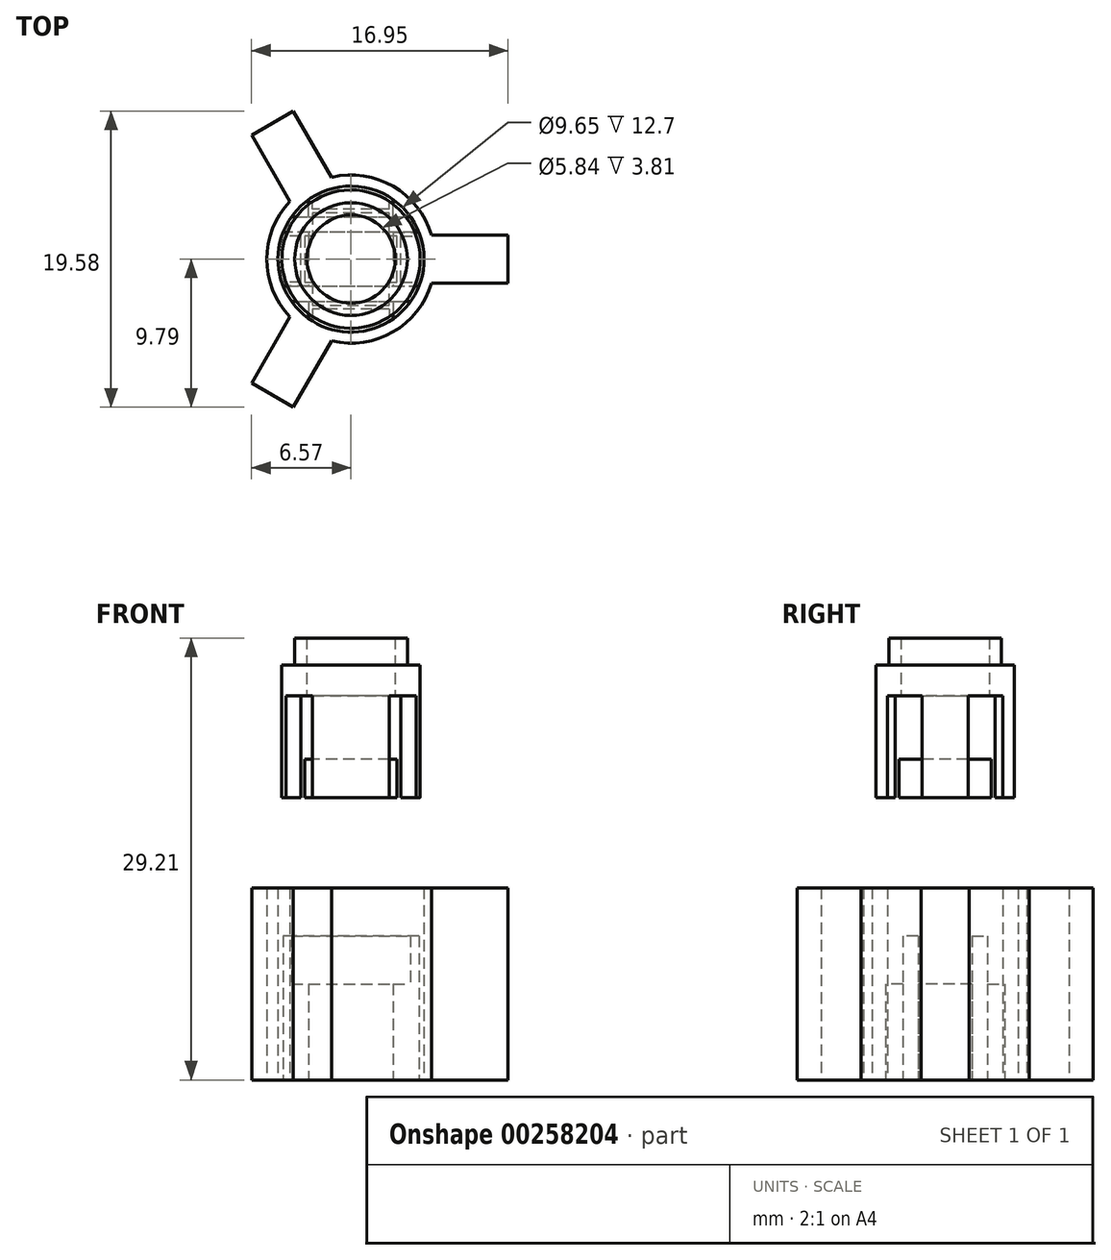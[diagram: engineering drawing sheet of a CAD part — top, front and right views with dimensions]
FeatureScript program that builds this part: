
annotation { "Feature Type Name" : "Feature", "Feature Type Description" : "" }
export const myFeature = defineFeature(function(context is Context, id is Id, definition is map)
    precondition{}
    {
        {
            var Q0;
            Q0=qCreatedBy(makeId("Top.planeOp"),FACE);
            var sketch = newSketch(context, id + "F0", { "sketchPlane" : qUnion([Q0])});
            skCircle(sketch, "E0", {"center": v(0, 0) * mm, "radius": 4.57 * mm});
            skCircle(sketch, "E1", {"center": v(0, 0) * mm, "radius": 2.92 * mm});
            skSolve(sketch);
        }
        {
            var Q0;
            Q0 = qSketchRegion(id + "F0", true);
            extrude(context, id + "F1", {"entities" : qUnion([Q0]), "depth" : 3.8 * mm});
        }
        {
            var Q0;
            Q0=makeQuery(id+"F1.opExtrude","CAP_FACE",FACE,{"disambiguationData":[OSD([sQuery(id+"F0.wireOp",EDGE,"E0"),sQuery(id+"F0.wireOp",EDGE,"E1")])],"isStart":false});
            var sketch = newSketch(context, id + "F2", { "sketchPlane" : qUnion([Q0])});
            skCircle(sketch, "E2.0", {"center": v(0, 0) * mm, "radius": 4.57 * mm});
            skCircle(sketch, "E3", {"center": v(0, 0) * mm, "radius": 3.72 * mm});
            skSolve(sketch);
        }
        {
            var Q0;
            Q0 = qSketchRegion(id + "F2", true);
            extrude(context, id + "F3", {"entities" : qUnion([Q0]), "operationType" : NewBodyOperationType.REMOVE, "oppositeDirection" : true, "depth" : 1.78 * mm});
        }
        {
            var Q0;
            Q0=makeQuery(id+"F1.opExtrude","CAP_FACE",FACE,{"disambiguationData":[OSD([sQuery(id+"F0.wireOp",EDGE,"E0"),sQuery(id+"F0.wireOp",EDGE,"E1")])],"isStart":true});
            var sketch = newSketch(context, id + "F4", { "sketchPlane" : qUnion([Q0])});
            skCircle(sketch, "E4.0", {"center": v(0, 0) * mm, "radius": 2.92 * mm, "construction": true});
            skArc(sketch, "E5.0", {"start": v(-4.31, 1.52) * mm, "mid": v(-4.57, 0) * mm, "end": v(-4.31, -1.52) * mm});
            skLineSegment(sketch, "E6.bottom", {"start": v(-3.3, 3.3) * mm, "end": v(3.3, 3.3) * mm, "construction": true});
            skLineSegment(sketch, "E6.top", {"start": v(-3.3, -3.3) * mm, "end": v(3.3, -3.3) * mm, "construction": true});
            skLineSegment(sketch, "E6.left", {"start": v(-3.3, 3.3) * mm, "end": v(-3.3, -3.3) * mm, "construction": true});
            skLineSegment(sketch, "E6.right", {"start": v(3.3, 3.3) * mm, "end": v(3.3, -3.3) * mm, "construction": true});
            skPoint(sketch, "E7.positionSnap0", {"position": v(-3.3, 0) * mm});
            skPoint(sketch, "E7.positionSnap1", {"position": v(0, 3.3) * mm});
            skLineSegment(sketch, "E8.bottom", {"start": v(-3.3, 1.52) * mm, "end": v(-4.31, 1.52) * mm});
            skLineSegment(sketch, "E8.top", {"start": v(-3.3, -1.52) * mm, "end": v(-4.31, -1.52) * mm});
            skLineSegment(sketch, "E8.left", {"start": v(-3.3, 1.52) * mm, "end": v(-3.3, -1.52) * mm});
            skLineSegment(sketch, "E9.bottom", {"start": v(2.54, 3.3) * mm, "end": v(2.54, 3.8) * mm});
            skLineSegment(sketch, "E9.top", {"start": v(-2.54, 3.3) * mm, "end": v(-2.54, 3.8) * mm});
            skLineSegment(sketch, "E9.left", {"start": v(2.54, 3.3) * mm, "end": v(-2.54, 3.3) * mm});
            skArc(sketch, "E10.trimOffspring", {"start": v(2.54, 3.8) * mm, "mid": v(0, 4.57) * mm, "end": v(-2.54, 3.8) * mm});
            skLineSegment(sketch, "E11", {"start": v(0, 0) * mm, "end": v(-3.3, 0) * mm, "construction": true});
            skLineSegment(sketch, "E12", {"start": v(0, 0) * mm, "end": v(0, 3.3) * mm, "construction": true});
            skPoint(sketch, "E13.MirrorP", {"position": v(3.3, 0) * mm});
            skLineSegment(sketch, "E14.MirrorCS", {"start": v(3.3, 1.52) * mm, "end": v(4.31, 1.52) * mm});
            skLineSegment(sketch, "E15.MirrorCS", {"start": v(3.3, -1.52) * mm, "end": v(4.31, -1.52) * mm});
            skArc(sketch, "E16.MirrorCS", {"start": v(4.31, 1.52) * mm, "mid": v(4.57, 0) * mm, "end": v(4.31, -1.52) * mm});
            skLineSegment(sketch, "E17.MirrorCS", {"start": v(3.3, 1.52) * mm, "end": v(3.3, -1.52) * mm});
            skPoint(sketch, "E18.MirrorP", {"position": v(0, -3.3) * mm});
            skLineSegment(sketch, "E19.MirrorCS", {"start": v(2.54, -3.3) * mm, "end": v(2.54, -3.8) * mm});
            skLineSegment(sketch, "E20.MirrorCS", {"start": v(2.54, -3.3) * mm, "end": v(-2.54, -3.3) * mm});
            skLineSegment(sketch, "E21.MirrorCS", {"start": v(-2.54, -3.3) * mm, "end": v(-2.54, -3.8) * mm});
            skArc(sketch, "E22.MirrorCS", {"start": v(2.54, -3.8) * mm, "mid": v(0, -4.57) * mm, "end": v(-2.54, -3.8) * mm});
            skSolve(sketch);
        }
        {
            var Q0;
            Q0 = qSketchRegion(id + "F4", true);
            extrude(context, id + "F5", {"entities" : qUnion([Q0]), "operationType" : NewBodyOperationType.ADD, "depth" : 3.56 * mm});
        }
        {
            var Q0;
            Q0=makeQuery(id+"F5.opExtrude","CAP_FACE",FACE,{"disambiguationData":[OSD([sQuery(id+"F4.wireOp",EDGE,"E19.MirrorCS"),sQuery(id+"F4.wireOp",EDGE,"E20.MirrorCS"),sQuery(id+"F4.wireOp",EDGE,"E21.MirrorCS"),sQuery(id+"F4.wireOp",EDGE,"E22.MirrorCS")])],"isStart":false});
            var Q1;
            Q1=makeQuery(id+"F5.opExtrude","CAP_FACE",FACE,{"disambiguationData":[OSD([sQuery(id+"F4.wireOp",EDGE,"E9.bottom"),sQuery(id+"F4.wireOp",EDGE,"E9.top"),sQuery(id+"F4.wireOp",EDGE,"E9.left"),sQuery(id+"F4.wireOp",EDGE,"E10.trimOffspring")])],"isStart":false});
            var Q2;
            Q2=makeQuery(id+"F5.opExtrude","CAP_FACE",FACE,{"disambiguationData":[OSD([sQuery(id+"F4.wireOp",EDGE,"E5.0"),sQuery(id+"F4.wireOp",EDGE,"E8.bottom"),sQuery(id+"F4.wireOp",EDGE,"E8.top"),sQuery(id+"F4.wireOp",EDGE,"E8.left")])],"isStart":false});
            var Q3;
            Q3=makeQuery(id+"F5.opExtrude","CAP_FACE",FACE,{"disambiguationData":[OSD([sQuery(id+"F4.wireOp",EDGE,"E14.MirrorCS"),sQuery(id+"F4.wireOp",EDGE,"E15.MirrorCS"),sQuery(id+"F4.wireOp",EDGE,"E16.MirrorCS"),sQuery(id+"F4.wireOp",EDGE,"E17.MirrorCS")])],"isStart":false});
            extrude(context, id + "F6", {"entities" : qUnion([Q0, Q1, Q2, Q3]), "operationType" : NewBodyOperationType.ADD, "depth" : 3.17 * mm});
        }
        {
            var Q0;
            Q0=makeQuery(id+"F6.opExtrude","CAP_FACE",FACE,{"disambiguationData":[OSD([sQuery(id+"F4.wireOp",EDGE,"E14.MirrorCS"),sQuery(id+"F4.wireOp",EDGE,"E15.MirrorCS"),sQuery(id+"F4.wireOp",EDGE,"E16.MirrorCS"),sQuery(id+"F4.wireOp",EDGE,"E17.MirrorCS")])],"isStart":false});
            var sketch = newSketch(context, id + "F7", { "sketchPlane" : qUnion([Q0])});
            skPoint(sketch, "E23.0", {"position": v(0, 3.3) * mm});
            skLineSegment(sketch, "E24.0", {"start": v(2.54, -3.3) * mm, "end": v(-2.54, -3.3) * mm, "construction": true});
            skPoint(sketch, "E25.0", {"position": v(-3.3, 0) * mm});
            skPoint(sketch, "E26.0", {"position": v(3.3, 0) * mm});
            skLineSegment(sketch, "E27", {"start": v(-3.3, 0) * mm, "end": v(3.3, 0) * mm, "construction": true});
            skLineSegment(sketch, "E28.bottom", {"start": v(-3.05, 3.05) * mm, "end": v(3.05, 3.05) * mm, "construction": true});
            skLineSegment(sketch, "E28.top", {"start": v(-3.05, -3.05) * mm, "end": v(3.05, -3.05) * mm, "construction": true});
            skLineSegment(sketch, "E28.left", {"start": v(-3.05, 3.05) * mm, "end": v(-3.05, -3.05) * mm, "construction": true});
            skLineSegment(sketch, "E28.right", {"start": v(3.05, 3.05) * mm, "end": v(3.05, -3.05) * mm, "construction": true});
            skPoint(sketch, "E29", {"position": v(0, 0) * mm});
            skPoint(sketch, "E29.positionSnap0", {"position": v(-3.05, 0) * mm});
            skPoint(sketch, "E29.positionSnap1", {"position": v(0, 3.05) * mm});
            skPoint(sketch, "E30.0", {"position": v(-3.3, 1.52) * mm});
            skPoint(sketch, "E31.0", {"position": v(-3.3, -1.52) * mm});
            skPoint(sketch, "E32.0", {"position": v(-2.54, 3.3) * mm});
            skPoint(sketch, "E33.0", {"position": v(2.54, 3.3) * mm});
            skPoint(sketch, "E34.0", {"position": v(3.3, -1.52) * mm});
            skPoint(sketch, "E35.0", {"position": v(3.3, 1.52) * mm});
            skLineSegment(sketch, "E36", {"start": v(-2.54, 3.3) * mm, "end": v(-2.54, -3.3) * mm, "construction": true});
            skLineSegment(sketch, "E37", {"start": v(2.54, 3.3) * mm, "end": v(2.54, -3.3) * mm, "construction": true});
            skLineSegment(sketch, "E38", {"start": v(3.3, -1.52) * mm, "end": v(-3.3, -1.52) * mm, "construction": true});
            skLineSegment(sketch, "E39", {"start": v(-3.3, 1.52) * mm, "end": v(3.3, 1.52) * mm, "construction": true});
            skLineSegment(sketch, "E40", {"start": v(-3.05, 1.52) * mm, "end": v(-2.54, 1.52) * mm});
            skLineSegment(sketch, "E41", {"start": v(-2.54, 1.52) * mm, "end": v(-2.54, 3.05) * mm});
            skLineSegment(sketch, "E42", {"start": v(-2.54, 3.05) * mm, "end": v(2.54, 3.05) * mm});
            skLineSegment(sketch, "E43", {"start": v(2.54, 3.05) * mm, "end": v(2.54, 1.52) * mm});
            skLineSegment(sketch, "E44", {"start": v(2.54, 1.52) * mm, "end": v(3.05, 1.52) * mm});
            skLineSegment(sketch, "E45", {"start": v(3.05, 1.52) * mm, "end": v(3.05, -1.52) * mm});
            skLineSegment(sketch, "E46", {"start": v(3.05, -1.52) * mm, "end": v(2.54, -1.52) * mm});
            skLineSegment(sketch, "E47", {"start": v(2.54, -1.52) * mm, "end": v(2.54, -3.05) * mm});
            skLineSegment(sketch, "E48", {"start": v(2.54, -3.05) * mm, "end": v(-2.54, -3.05) * mm});
            skLineSegment(sketch, "E49", {"start": v(-2.54, -3.05) * mm, "end": v(-2.54, -1.52) * mm});
            skLineSegment(sketch, "E50", {"start": v(-2.54, -1.52) * mm, "end": v(-3.05, -1.52) * mm});
            skLineSegment(sketch, "E51", {"start": v(-3.05, -1.52) * mm, "end": v(-3.05, 1.52) * mm});
            skSolve(sketch);
        }
        {
            var Q0;
            Q0 = qSketchRegion(id + "F7", true);
            extrude(context, id + "F8", {"entities" : qUnion([Q0]), "oppositeDirection" : true, "depth" : 2.54 * mm});
        }
        {
            var Q0;
            Q0=qCreatedBy(makeId("Top.planeOp"),FACE);
            cPlane(context, id + "F9", {"entities" : qUnion([Q0]), "cplaneType" : CPlaneType.OFFSET, "offset" : 25.4 * mm, "oppositeDirection" : true, "width" : 152.4 * mm, "height" : 152.4 * mm});
        }
        {
            var Q0;
            Q0=qCreatedBy(id+"F9.planeOp",FACE);
            var sketch = newSketch(context, id + "F10", { "sketchPlane" : qUnion([Q0])});
            skArc(sketch, "E52", {"start": v(-4.04, 3.82) * mm, "mid": v(-5.56, 0) * mm, "end": v(-4.04, -3.82) * mm});
            skLineSegment(sketch, "E53", {"start": v(0, 0) * mm, "end": v(0, 6.2) * mm, "construction": true});
            skLineSegment(sketch, "E54", {"start": v(0, 0) * mm, "end": v(-6.03, 0) * mm, "construction": true});
            skLineSegment(sketch, "E55.bottom", {"start": v(5.32, 1.59) * mm, "end": v(10.38, 1.59) * mm});
            skLineSegment(sketch, "E55.top", {"start": v(5.32, -1.59) * mm, "end": v(10.38, -1.59) * mm});
            skLineSegment(sketch, "E55.right", {"start": v(10.38, 1.59) * mm, "end": v(10.38, -1.59) * mm});
            skPoint(sketch, "E56", {"position": v(5.3, 0) * mm});
            skLineSegment(sketch, "E57.1.0", {"start": v(-1.29, 5.4) * mm, "end": v(-3.82, 9.79) * mm});
            skLineSegment(sketch, "E57.1.1", {"start": v(-6.57, 8.2) * mm, "end": v(-3.82, 9.79) * mm});
            skLineSegment(sketch, "E57.1.2", {"start": v(-4.04, 3.82) * mm, "end": v(-6.57, 8.2) * mm});
            skLineSegment(sketch, "E57.2.0", {"start": v(-4.04, -3.82) * mm, "end": v(-6.57, -8.2) * mm});
            skLineSegment(sketch, "E57.2.1", {"start": v(-3.82, -9.79) * mm, "end": v(-6.57, -8.2) * mm});
            skLineSegment(sketch, "E57.2.2", {"start": v(-1.29, -5.4) * mm, "end": v(-3.82, -9.79) * mm});
            skArc(sketch, "E58.trimOffspring", {"start": v(-1.29, -5.4) * mm, "mid": v(2.78, -4.81) * mm, "end": v(5.32, -1.59) * mm});
            skArc(sketch, "E59.trimOffspring", {"start": v(5.32, 1.59) * mm, "mid": v(2.78, 4.81) * mm, "end": v(-1.29, 5.4) * mm});
            skPoint(sketch, "E60.orphan", {"position": v(5.3, 1.59) * mm});
            skPoint(sketch, "E61.orphan", {"position": v(5.3, -1.59) * mm});
            skPoint(sketch, "E62.orphan", {"position": v(-4.03, -3.8) * mm});
            skPoint(sketch, "E63.orphan", {"position": v(-1.28, -5.39) * mm});
            skPoint(sketch, "E64.orphan", {"position": v(-1.28, 5.39) * mm});
            skPoint(sketch, "E65.orphan", {"position": v(-4.03, 3.8) * mm});
            skLineSegment(sketch, "E66.0", {"start": v(-2.8, 1.78) * mm, "end": v(-2.8, -1.78) * mm});
            skLineSegment(sketch, "E67.0", {"start": v(-2.8, 1.78) * mm, "end": v(-4.49, 1.78) * mm});
            skLineSegment(sketch, "E68.0", {"start": v(-2.8, -1.78) * mm, "end": v(-4.49, -1.78) * mm});
            skArc(sketch, "E69", {"start": v(-2.8, -3.93) * mm, "mid": v(0, -4.82) * mm, "end": v(2.8, -3.93) * mm});
            skLineSegment(sketch, "E70.0", {"start": v(-2.8, -2.8) * mm, "end": v(-2.8, -3.93) * mm});
            skLineSegment(sketch, "E71.0", {"start": v(-2.8, -2.8) * mm, "end": v(2.8, -2.8) * mm});
            skLineSegment(sketch, "E72.MirrorCS", {"start": v(-5.59, 0) * mm, "end": v(-5.59, 6.2) * mm, "construction": true});
            skLineSegment(sketch, "E73.MirrorCS", {"start": v(2.8, -2.8) * mm, "end": v(2.8, -3.93) * mm});
            skArc(sketch, "E74.trimOffspring", {"start": v(-4.49, 1.78) * mm, "mid": v(-4.82, 0) * mm, "end": v(-4.49, -1.78) * mm});
            skLineSegment(sketch, "E75.MirrorCS", {"start": v(-2.8, 2.8) * mm, "end": v(2.8, 2.8) * mm});
            skLineSegment(sketch, "E76.MirrorCS", {"start": v(2.8, 2.8) * mm, "end": v(2.8, 3.93) * mm});
            skLineSegment(sketch, "E77.MirrorCS", {"start": v(-2.8, 2.8) * mm, "end": v(-2.8, 3.93) * mm});
            skArc(sketch, "E78.MirrorCS", {"start": v(-2.8, 3.93) * mm, "mid": v(0, 4.82) * mm, "end": v(2.8, 3.93) * mm});
            skLineSegment(sketch, "E79.MirrorCS", {"start": v(2.8, -1.78) * mm, "end": v(4.49, -1.78) * mm});
            skLineSegment(sketch, "E80.MirrorCS", {"start": v(2.8, 1.78) * mm, "end": v(2.8, -1.78) * mm});
            skLineSegment(sketch, "E81.MirrorCS", {"start": v(2.8, 1.78) * mm, "end": v(4.49, 1.78) * mm});
            skArc(sketch, "E82.MirrorCS", {"start": v(4.49, 1.78) * mm, "mid": v(4.82, 0) * mm, "end": v(4.49, -1.78) * mm});
            skSolve(sketch);
        }
        {
            var Q0;
            Q0 = qSketchRegion(id + "F10", true);
            extrude(context, id + "F11", {"entities" : qUnion([Q0]), "depth" : 6.35 * mm});
        }
        {
            var Q0;
            Q0=makeQuery(id+"F11.opExtrude","CAP_FACE",FACE,{"disambiguationData":[OSD([sQuery(id+"F10.wireOp",EDGE,"db18d521-57b8-4300-b0c5-4cde51a523bd.0.0"),sQuery(id+"F10.wireOp",EDGE,"db18d521-57b8-4300-b0c5-4cde51a523bd.0.3"),sQuery(id+"F10.wireOp",EDGE,"db18d521-57b8-4300-b0c5-4cde51a523bd.0.6"),sQuery(id+"F10.wireOp",EDGE,"db18d521-57b8-4300-b0c5-4cde51a523bd.0.9"),sQuery(id+"F10.wireOp",EDGE,"369de0dd-4191-417d-bcee-15261e193363.0"),sQuery(id+"F10.wireOp",EDGE,"E52"),sQuery(id+"F10.wireOp",EDGE,"kX5wIPr1-428x-K9z2-gXJk-3hD54hDqaICx"),sQuery(id+"F10.wireOp",EDGE,"egBcWlUM-x16y-42HG-bm2Q-WMoGCDpll3w8"),sQuery(id+"F10.wireOp",EDGE,"77dcda4e-ead9-4f28-8145-114dee90182b0.MirrorCS"),sQuery(id+"F10.wireOp",EDGE,"77dcda4e-ead9-4f28-8145-114dee90182b1.MirrorCS"),sQuery(id+"F10.wireOp",EDGE,"fe240c59-e6ec-4a6d-bc8b-0338589bbb20.trimOffspring"),sQuery(id+"F10.wireOp",EDGE,"713e28b8-72cb-480b-ac16-a4ad6be82ba40.MirrorCS"),sQuery(id+"F10.wireOp",EDGE,"713e28b8-72cb-480b-ac16-a4ad6be82ba41.MirrorCS"),sQuery(id+"F10.wireOp",EDGE,"713e28b8-72cb-480b-ac16-a4ad6be82ba42.MirrorCS"),sQuery(id+"F10.wireOp",EDGE,"713e28b8-72cb-480b-ac16-a4ad6be82ba43.MirrorCS"),sQuery(id+"F10.wireOp",EDGE,"104ba62b-27fc-46a6-bafd-026f3a624c96.trimOffspring"),sQuery(id+"F10.wireOp",EDGE,"f2ccea3b-76f7-4db3-a6ea-49b77455acce.trimOffspring"),sQuery(id+"F10.wireOp",EDGE,"E55.bottom"),sQuery(id+"F10.wireOp",EDGE,"E55.top"),sQuery(id+"F10.wireOp",EDGE,"E55.right"),sQuery(id+"F10.wireOp",EDGE,"E57.1.0"),sQuery(id+"F10.wireOp",EDGE,"E57.1.1"),sQuery(id+"F10.wireOp",EDGE,"E57.1.2"),sQuery(id+"F10.wireOp",EDGE,"E57.2.0"),sQuery(id+"F10.wireOp",EDGE,"E57.2.1"),sQuery(id+"F10.wireOp",EDGE,"E57.2.2"),sQuery(id+"F10.wireOp",EDGE,"E58.trimOffspring"),sQuery(id+"F10.wireOp",EDGE,"E59.trimOffspring")])],"isStart":false});
            var sketch = newSketch(context, id + "F12", { "sketchPlane" : qUnion([Q0])});
            skLineSegment(sketch, "E83.0.0", {"start": v(10.38, 1.59) * mm, "end": v(5.32, 1.59) * mm});
            skArc(sketch, "E83.0.1", {"start": v(5.32, 1.59) * mm, "mid": v(2.78, 4.81) * mm, "end": v(-1.29, 5.4) * mm});
            skLineSegment(sketch, "E83.0.2", {"start": v(-1.29, 5.4) * mm, "end": v(-3.82, 9.79) * mm});
            skLineSegment(sketch, "E83.0.3", {"start": v(-3.82, 9.79) * mm, "end": v(-6.57, 8.2) * mm});
            skLineSegment(sketch, "E83.0.4", {"start": v(-6.57, 8.2) * mm, "end": v(-4.04, 3.82) * mm});
            skArc(sketch, "E83.0.5", {"start": v(-4.04, 3.82) * mm, "mid": v(-5.56, 0) * mm, "end": v(-4.04, -3.82) * mm});
            skLineSegment(sketch, "E83.0.6", {"start": v(-4.04, -3.82) * mm, "end": v(-6.57, -8.2) * mm});
            skLineSegment(sketch, "E83.0.7", {"start": v(-6.57, -8.2) * mm, "end": v(-3.82, -9.79) * mm});
            skLineSegment(sketch, "E83.0.8", {"start": v(-3.82, -9.79) * mm, "end": v(-1.29, -5.4) * mm});
            skArc(sketch, "E83.0.9", {"start": v(-1.29, -5.4) * mm, "mid": v(2.78, -4.81) * mm, "end": v(5.32, -1.59) * mm});
            skLineSegment(sketch, "E83.0.10", {"start": v(5.32, -1.59) * mm, "end": v(10.38, -1.59) * mm});
            skLineSegment(sketch, "E83.0.11", {"start": v(10.38, -1.59) * mm, "end": v(10.38, 1.59) * mm});
            skArc(sketch, "E84.0", {"start": v(-4.49, 1.78) * mm, "mid": v(-4.82, 0) * mm, "end": v(-4.49, -1.78) * mm, "construction": true});
            skArc(sketch, "E85.0", {"start": v(-2.8, 3.93) * mm, "mid": v(0, 4.82) * mm, "end": v(2.8, 3.93) * mm, "construction": true});
            skArc(sketch, "E86.0", {"start": v(4.49, 1.78) * mm, "mid": v(4.82, 0) * mm, "end": v(4.49, -1.78) * mm, "construction": true});
            skArc(sketch, "E87.0", {"start": v(-2.8, -3.93) * mm, "mid": v(0, -4.82) * mm, "end": v(2.8, -3.93) * mm, "construction": true});
            skArc(sketch, "E88", {"start": v(-3.93, -2.8) * mm, "mid": v(0, -4.82) * mm, "end": v(3.93, -2.8) * mm});
            skLineSegment(sketch, "E89.0", {"start": v(-2.8, -2.8) * mm, "end": v(2.8, -2.8) * mm, "construction": true});
            skLineSegment(sketch, "E90.0", {"start": v(-2.8, -1.78) * mm, "end": v(-4.49, -1.78) * mm, "construction": true});
            skLineSegment(sketch, "E91.0", {"start": v(2.8, -1.78) * mm, "end": v(4.49, -1.78) * mm, "construction": true});
            skLineSegment(sketch, "E92.bottom", {"start": v(-4.49, -1.78) * mm, "end": v(4.49, -1.78) * mm});
            skLineSegment(sketch, "E92.top", {"start": v(-3.93, -2.8) * mm, "end": v(3.93, -2.8) * mm});
            skPoint(sketch, "E92.right.end.orphan", {"position": v(4.49, -2.8) * mm});
            skArc(sketch, "E93.trimOffspring", {"start": v(4.49, -1.78) * mm, "mid": v(4.82, 0) * mm, "end": v(4.49, 1.78) * mm});
            skLineSegment(sketch, "E94.0", {"start": v(-2.8, 1.78) * mm, "end": v(-4.49, 1.78) * mm, "construction": true});
            skLineSegment(sketch, "E95.0", {"start": v(-2.8, 2.8) * mm, "end": v(2.8, 2.8) * mm, "construction": true});
            skLineSegment(sketch, "E96.0", {"start": v(2.8, 1.78) * mm, "end": v(4.49, 1.78) * mm, "construction": true});
            skLineSegment(sketch, "E97.bottom", {"start": v(-4.49, 1.78) * mm, "end": v(4.49, 1.78) * mm});
            skLineSegment(sketch, "E97.top", {"start": v(-3.93, 2.8) * mm, "end": v(3.93, 2.8) * mm});
            skArc(sketch, "E98.trimOffspring", {"start": v(-4.49, 1.78) * mm, "mid": v(-4.82, 0) * mm, "end": v(-4.49, -1.78) * mm});
            skPoint(sketch, "E99.orphan", {"position": v(4.49, 2.8) * mm});
            skArc(sketch, "E100.trimOffspring", {"start": v(3.93, 2.8) * mm, "mid": v(0, 4.82) * mm, "end": v(-3.93, 2.8) * mm});
            skSolve(sketch);
        }
        {
            var Q0;
            Q0 = qSketchRegion(id + "F12", true);
            extrude(context, id + "F13", {"entities" : qUnion([Q0]), "operationType" : NewBodyOperationType.ADD, "depth" : 3.17 * mm});
        }
        {
            var Q0;
            Q0=makeQuery(id+"F13.opExtrude","CAP_FACE",FACE,{"disambiguationData":[OSD([sQuery(id+"F12.wireOp",EDGE,"E83.0.0"),sQuery(id+"F12.wireOp",EDGE,"E83.0.1"),sQuery(id+"F12.wireOp",EDGE,"E83.0.2"),sQuery(id+"F12.wireOp",EDGE,"E83.0.3"),sQuery(id+"F12.wireOp",EDGE,"E83.0.4"),sQuery(id+"F12.wireOp",EDGE,"E83.0.5"),sQuery(id+"F12.wireOp",EDGE,"E83.0.6"),sQuery(id+"F12.wireOp",EDGE,"E83.0.7"),sQuery(id+"F12.wireOp",EDGE,"E83.0.8"),sQuery(id+"F12.wireOp",EDGE,"E83.0.9"),sQuery(id+"F12.wireOp",EDGE,"E83.0.10"),sQuery(id+"F12.wireOp",EDGE,"E83.0.11"),sQuery(id+"F12.wireOp",EDGE,"E88"),sQuery(id+"F12.wireOp",EDGE,"E92.bottom"),sQuery(id+"F12.wireOp",EDGE,"E92.top"),sQuery(id+"F12.wireOp",EDGE,"E93.trimOffspring"),sQuery(id+"F12.wireOp",EDGE,"E97.bottom"),sQuery(id+"F12.wireOp",EDGE,"E97.top"),sQuery(id+"F12.wireOp",EDGE,"E98.trimOffspring"),sQuery(id+"F12.wireOp",EDGE,"E100.trimOffspring")])],"isStart":false});
            var sketch = newSketch(context, id + "F14", { "sketchPlane" : qUnion([Q0])});
            skLineSegment(sketch, "E101.0.0", {"start": v(10.38, 1.59) * mm, "end": v(5.32, 1.59) * mm});
            skArc(sketch, "E101.0.1", {"start": v(5.32, 1.59) * mm, "mid": v(2.78, 4.81) * mm, "end": v(-1.29, 5.4) * mm});
            skLineSegment(sketch, "E101.0.2", {"start": v(-1.29, 5.4) * mm, "end": v(-3.82, 9.79) * mm});
            skLineSegment(sketch, "E101.0.3", {"start": v(-3.82, 9.79) * mm, "end": v(-6.57, 8.2) * mm});
            skLineSegment(sketch, "E101.0.4", {"start": v(-6.57, 8.2) * mm, "end": v(-4.04, 3.82) * mm});
            skArc(sketch, "E101.0.5", {"start": v(-4.04, 3.82) * mm, "mid": v(-5.56, 0) * mm, "end": v(-4.04, -3.82) * mm});
            skLineSegment(sketch, "E101.0.6", {"start": v(-4.04, -3.82) * mm, "end": v(-6.57, -8.2) * mm});
            skLineSegment(sketch, "E101.0.7", {"start": v(-6.57, -8.2) * mm, "end": v(-3.82, -9.79) * mm});
            skLineSegment(sketch, "E101.0.8", {"start": v(-3.82, -9.79) * mm, "end": v(-1.29, -5.4) * mm});
            skArc(sketch, "E101.0.9", {"start": v(-1.29, -5.4) * mm, "mid": v(2.78, -4.81) * mm, "end": v(5.32, -1.59) * mm});
            skLineSegment(sketch, "E101.0.10", {"start": v(5.32, -1.59) * mm, "end": v(10.38, -1.59) * mm});
            skLineSegment(sketch, "E101.0.11", {"start": v(10.38, -1.59) * mm, "end": v(10.38, 1.59) * mm});
            skCircle(sketch, "E102", {"center": v(0, 0) * mm, "radius": 4.82 * mm});
            skSolve(sketch);
        }
        {
            var Q0;
            Q0 = qSketchRegion(id + "F14", true);
            extrude(context, id + "F15", {"entities" : qUnion([Q0]), "operationType" : NewBodyOperationType.ADD, "depth" : 3.17 * mm});
        }
    });
